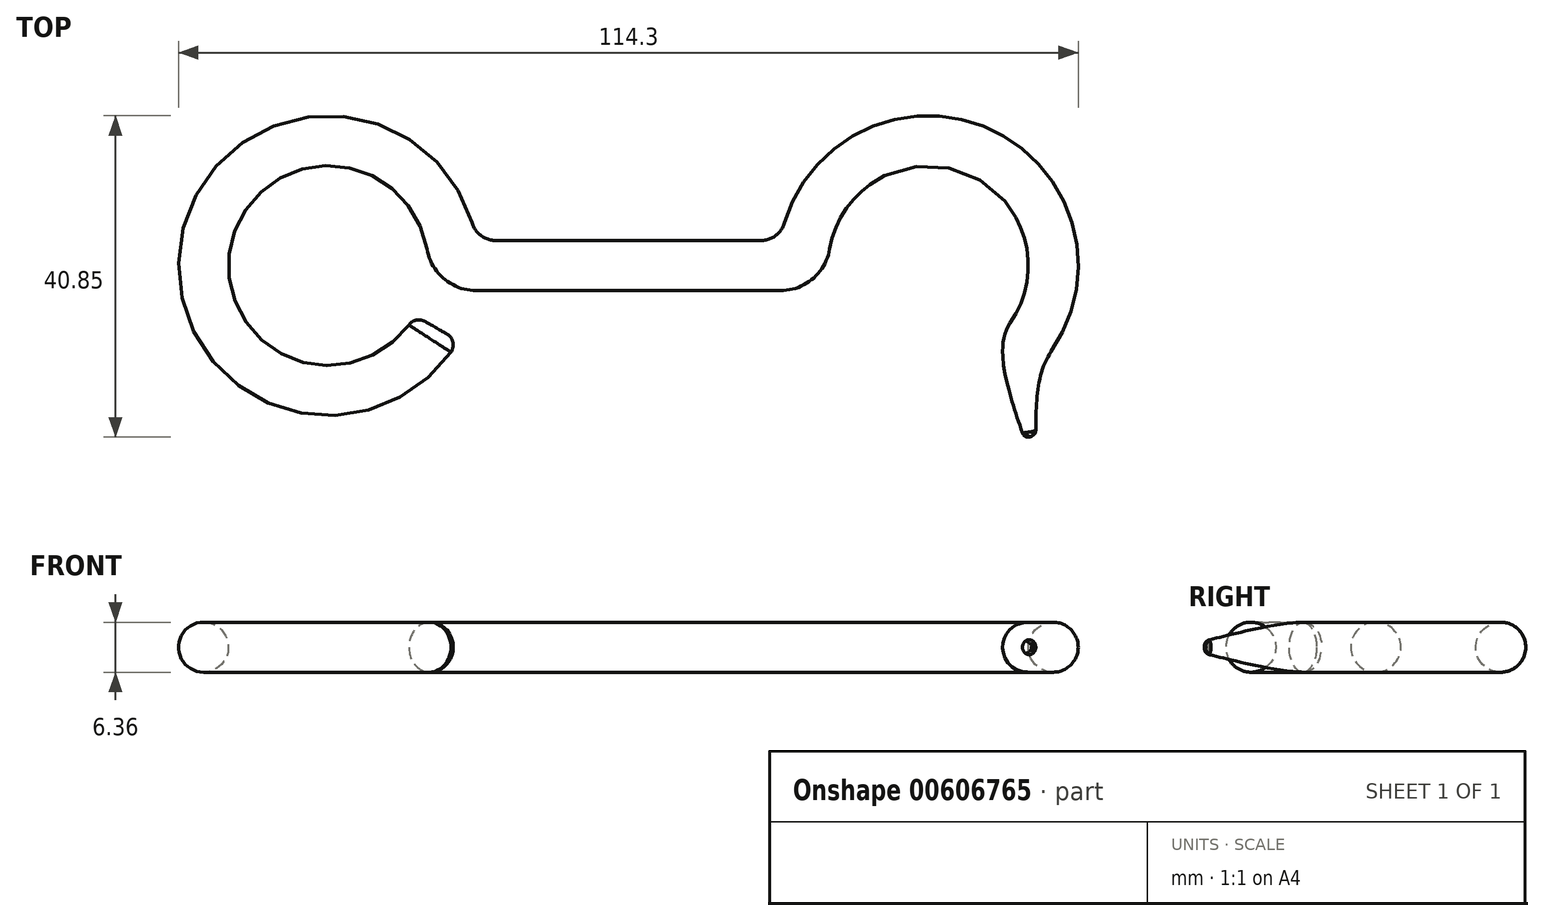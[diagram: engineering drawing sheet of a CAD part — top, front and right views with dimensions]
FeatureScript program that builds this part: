
annotation { "Feature Type Name" : "Feature", "Feature Type Description" : "" }
export const myFeature = defineFeature(function(context is Context, id is Id, definition is map)
    precondition{}
    {
        {
            var Q0;
            Q0=qCreatedBy(makeId("Top.planeOp"),FACE);
            var sketch = newSketch(context, id + "F0", { "sketchPlane" : qUnion([Q0])});
            skArc(sketch, "E0", {"start": v(12.52, 2.12) * mm, "mid": v(-12.5, 2.25) * mm, "end": v(11, -6.35) * mm});
            skArc(sketch, "E1", {"start": v(86.6, -7.28) * mm, "mid": v(81.02, 11.75) * mm, "end": v(63.68, 2.12) * mm});
            skArc(sketch, "E2.0", {"start": v(18.26, 5.44) * mm, "mid": v(-18.92, 2.22) * mm, "end": v(16.5, -9.53) * mm});
            skArc(sketch, "E3.0", {"start": v(91.8, -10.93) * mm, "mid": v(84.5, 17.15) * mm, "end": v(57.94, 5.44) * mm});
            skLineSegment(sketch, "E4.0", {"start": v(18.78, -3.18) * mm, "end": v(57.42, -3.18) * mm});
            skLineSegment(sketch, "E5.0", {"start": v(21.3, 3.18) * mm, "end": v(54.9, 3.18) * mm});
            skLineSegment(sketch, "E6", {"start": v(0, 0) * mm, "end": v(16.5, -9.53) * mm, "construction": true});
            skLineSegment(sketch, "E7", {"start": v(0, 0) * mm, "end": v(12.7, 0) * mm, "construction": true});
            skArc(sketch, "E8", {"start": v(18.26, 5.44) * mm, "mid": v(19.4, 3.8) * mm, "end": v(21.3, 3.18) * mm});
            skArc(sketch, "E9", {"start": v(54.9, 3.18) * mm, "mid": v(56.8, 3.8) * mm, "end": v(57.94, 5.44) * mm});
            skLineSegment(sketch, "E10", {"start": v(76.2, 0) * mm, "end": v(91.8, -10.93) * mm, "construction": true});
            skLineSegment(sketch, "E11", {"start": v(76.2, 0) * mm, "end": v(63.5, 0) * mm, "construction": true});
            skLineSegment(sketch, "E12", {"start": v(11, -6.35) * mm, "end": v(16.5, -9.53) * mm});
            skLineSegment(sketch, "E13", {"start": v(91.8, -10.93) * mm, "end": v(86.6, -7.28) * mm});
            skArc(sketch, "E14", {"start": v(12.52, 2.12) * mm, "mid": v(14.68, -1.67) * mm, "end": v(18.78, -3.18) * mm});
            skArc(sketch, "E15", {"start": v(57.42, -3.17) * mm, "mid": v(61.52, -1.67) * mm, "end": v(63.68, 2.12) * mm});
            skSolve(sketch);
        }
        {
            var Q0;
            Q0=makeQuery(id+"F0.imprint","IMPRINT",FACE,{"disambiguationData":[TD([[makeQuery(id+"F0.imprint","IMPRINT",EDGE,{"derivedFrom":sQuery(id+"F0.wireOp",EDGE,"E0")}),-1.0]])]});
            extrude(context, id + "F1", {"entities" : qUnion([Q0]), "depth" : 3.17 * mm, "offsetDistance" : 25.4 * mm, "hasSecondDirection" : true, "secondDirectionOppositeDirection" : true, "secondDirectionDepth" : 3.17 * mm});
        }
        {
            var Q0;
            Q0=makeQuery(id+"F1.opExtrude","CAP_EDGE",EDGE,{"disambiguationData":[OSD([sQuery(id+"F0.wireOp",EDGE,"E0")])],"isStart":false});
            var Q1;
            Q1=makeQuery(id+"F1.opExtrude","CAP_EDGE",EDGE,{"disambiguationData":[OSD([sQuery(id+"F0.wireOp",EDGE,"E2.0")])],"isStart":false});
            var Q2;
            Q2=makeQuery(id+"F1.opExtrude","CAP_EDGE",EDGE,{"disambiguationData":[OSD([sQuery(id+"F0.wireOp",EDGE,"E2.0")])],"isStart":true});
            var Q3;
            Q3=makeQuery(id+"F1.opExtrude","CAP_EDGE",EDGE,{"disambiguationData":[OSD([sQuery(id+"F0.wireOp",EDGE,"E0")])],"isStart":true});
            fillet(context, id + "F2", {"entities" : qUnion([Q0, Q1, Q2, Q3]), "radius" : 3.17 * mm, "tangentPropagation" : true, "allowEdgeOverflow" : false});
        }
        {
            var Q0;
            Q0=qCreatedBy(makeId("Top.planeOp"),FACE);
            var sketch = newSketch(context, id + "F3", { "sketchPlane" : qUnion([Q0])});
            skArc(sketch, "E16", {"start": v(89.17, -9.08) * mm, "mid": v(87.46, -15.43) * mm, "end": v(89.17, -21.78) * mm});
            skLineSegment(sketch, "E17", {"start": v(89.17, -21.78) * mm, "end": v(100.16, -15.43) * mm, "construction": true});
            skSolve(sketch);
        }
        {
            var Q0;
            Q0=sQuery(id+"F3.wireOp",EDGE,"E17");
            cPlane(context, id + "F4", {"entities" : qUnion([Q0]), "cplaneType" : CPlaneType.LINE_ANGLE, "offset" : 25.4 * mm, "angle" : 0 * degree, "width" : 152.4 * mm, "height" : 152.4 * mm});
        }
        {
            var Q0;
            Q0=qCreatedBy(id+"F4.planeOp",FACE);
            var sketch = newSketch(context, id + "F5", { "sketchPlane" : qUnion([Q0])});
            skCircle(sketch, "E18", {"center": v(-66.33, 0) * mm, "radius": 0.8 * mm});
            skSolve(sketch);
        }
        {
            var Q0;
            Q0=makeQuery(id+"F1.opExtrude","SWEPT_FACE",FACE,{"disambiguationData":[OSD([sQuery(id+"F0.wireOp",EDGE,"E13")])]});
            var Q1;
            Q1 = qSketchRegion(id + "F5", true);
            var Q2;
            Q2=sQuery(id+"F3.wireOp",EDGE,"E16");
            loft(context, id + "F6", {"operationType" : NewBodyOperationType.ADD, "startCondition" : LoftEndDerivativeType.NORMAL_TO_PROFILE, "startMagnitude" : 1, "sheetProfilesArray" : [{ "sheetProfileEntities" : qUnion([Q0]) }, { "sheetProfileEntities" : qUnion([Q1]) }], "guidesArray" : [{ "guideEntities" : qUnion([Q2]), "guideDerivativeType" : LoftGuideDerivativeType.DEFAULT, "guideDerivativeMagnitude" : 1 }]});
        }
        {
            var Q0;
            Q0=makeQuery(id+"F1.opExtrude","SWEPT_FACE",FACE,{"disambiguationData":[OSD([sQuery(id+"F0.wireOp",EDGE,"E12")])]});
            fillet(context, id + "F7", {"entities" : qUnion([Q0]), "radius" : 1.59 * mm, "tangentPropagation" : true, "allowEdgeOverflow" : false});
        }
        {
            var Q0;
            Q0=makeQuery(id+"F6.opLoft","CAP_FACE",FACE,{"disambiguationData":[OSD([makeQuery(id+"F5.imprint","IMPRINT",FACE,{"disambiguationData":[TD([[makeQuery(id+"F5.imprint","IMPRINT",EDGE,{"derivedFrom":sQuery(id+"F5.wireOp",EDGE,"E18")}),1.0]])]})])],"isStart":true});
            fillet(context, id + "F8", {"entities" : qUnion([Q0]), "radius" : 0.8 * mm, "tangentPropagation" : true, "allowEdgeOverflow" : false});
        }
    });
